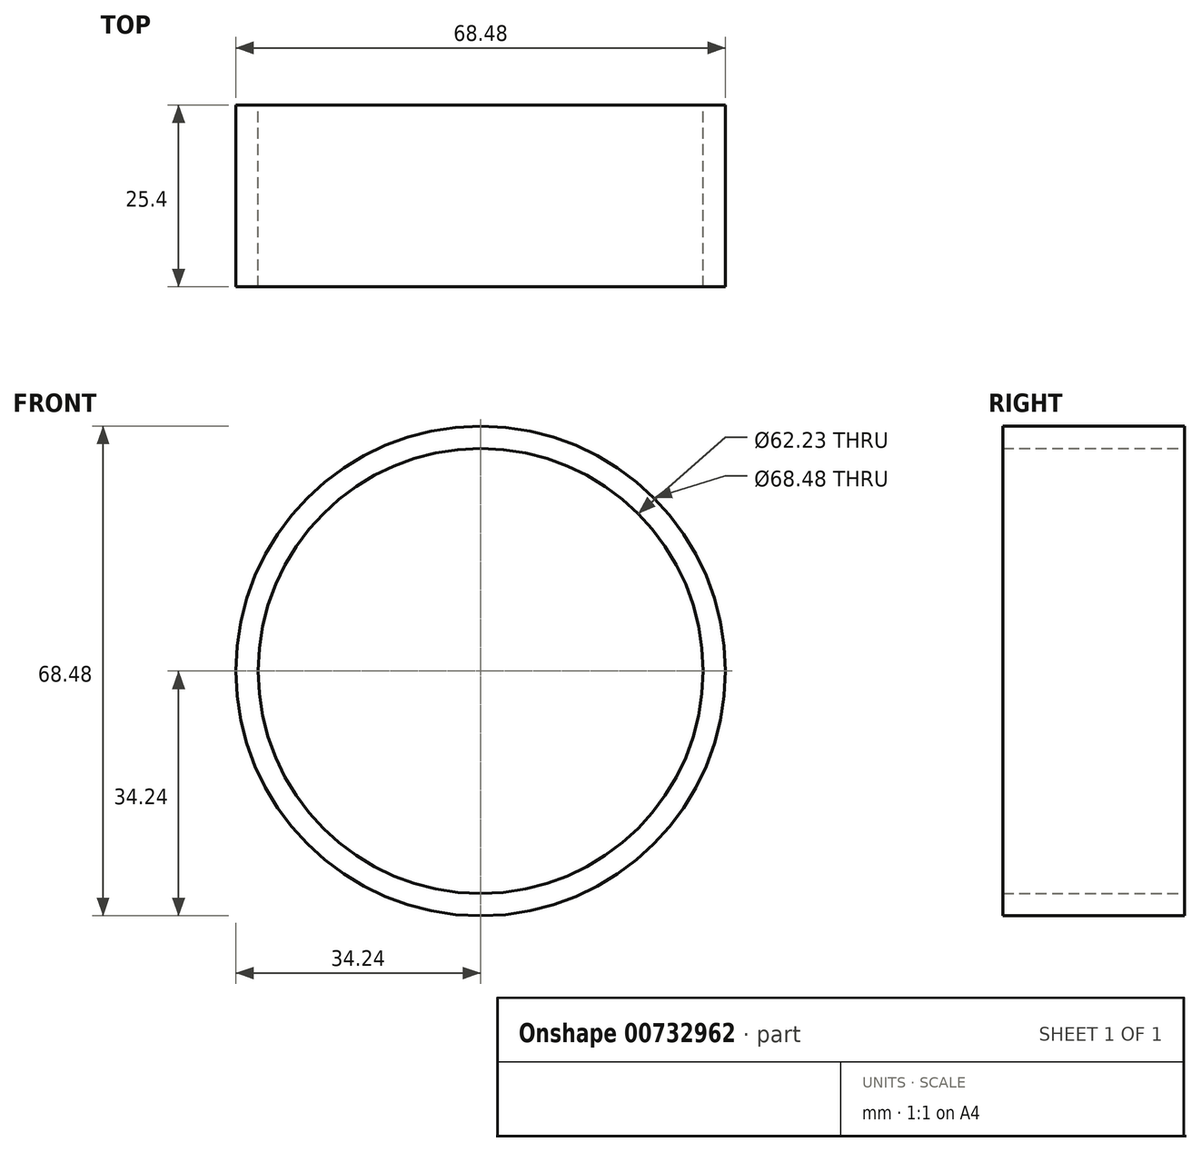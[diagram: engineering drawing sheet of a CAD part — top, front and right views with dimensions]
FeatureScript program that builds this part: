
annotation { "Feature Type Name" : "Feature", "Feature Type Description" : "" }
export const myFeature = defineFeature(function(context is Context, id is Id, definition is map)
    precondition{}
    {
        {
            var Q0;
            Q0=qCreatedBy(makeId("Front.planeOp"),FACE);
            var sketch = newSketch(context, id + "F0", { "sketchPlane" : qUnion([Q0])});
            skCircle(sketch, "E0", {"center": v(0, 0) * mm, "radius": 31.11 * mm});
            skSolve(sketch);
        }
        {
            var Q0;
            Q0=makeQuery(id+"F0.imprint","IMPRINT",FACE,{"disambiguationData":[TD([[makeQuery(id+"F0.imprint","IMPRINT",EDGE,{"derivedFrom":sQuery(id+"F0.wireOp",EDGE,"E0")}),1.0]])]});
            var sketch = newSketch(context, id + "F1", { "sketchPlane" : qUnion([Q0])});
            skCircle(sketch, "E1", {"center": v(0, 0) * mm, "radius": 34.24 * mm});
            skSolve(sketch);
        }
        {
            var Q0;
            Q0 = qSketchRegion(id + "F0", true);
            var Q1;
            Q1 = qSketchRegion(id + "F1", true);
            var Q2;
            Q2=sQuery(id+"F1.wireOp",EDGE,"E1");
            var Q3;
            Q3=sQuery(id+"F0.wireOp",EDGE,"E0");
            extrude(context, id + "F2", {"entities" : qUnion([Q0, Q1]), "bodyType" : ToolBodyType.SURFACE, "surfaceEntities" : qUnion([Q2, Q3]), "oppositeDirection" : true, "depth" : 25.4 * mm, "offsetDistance" : 25.4 * mm});
        }
    });
